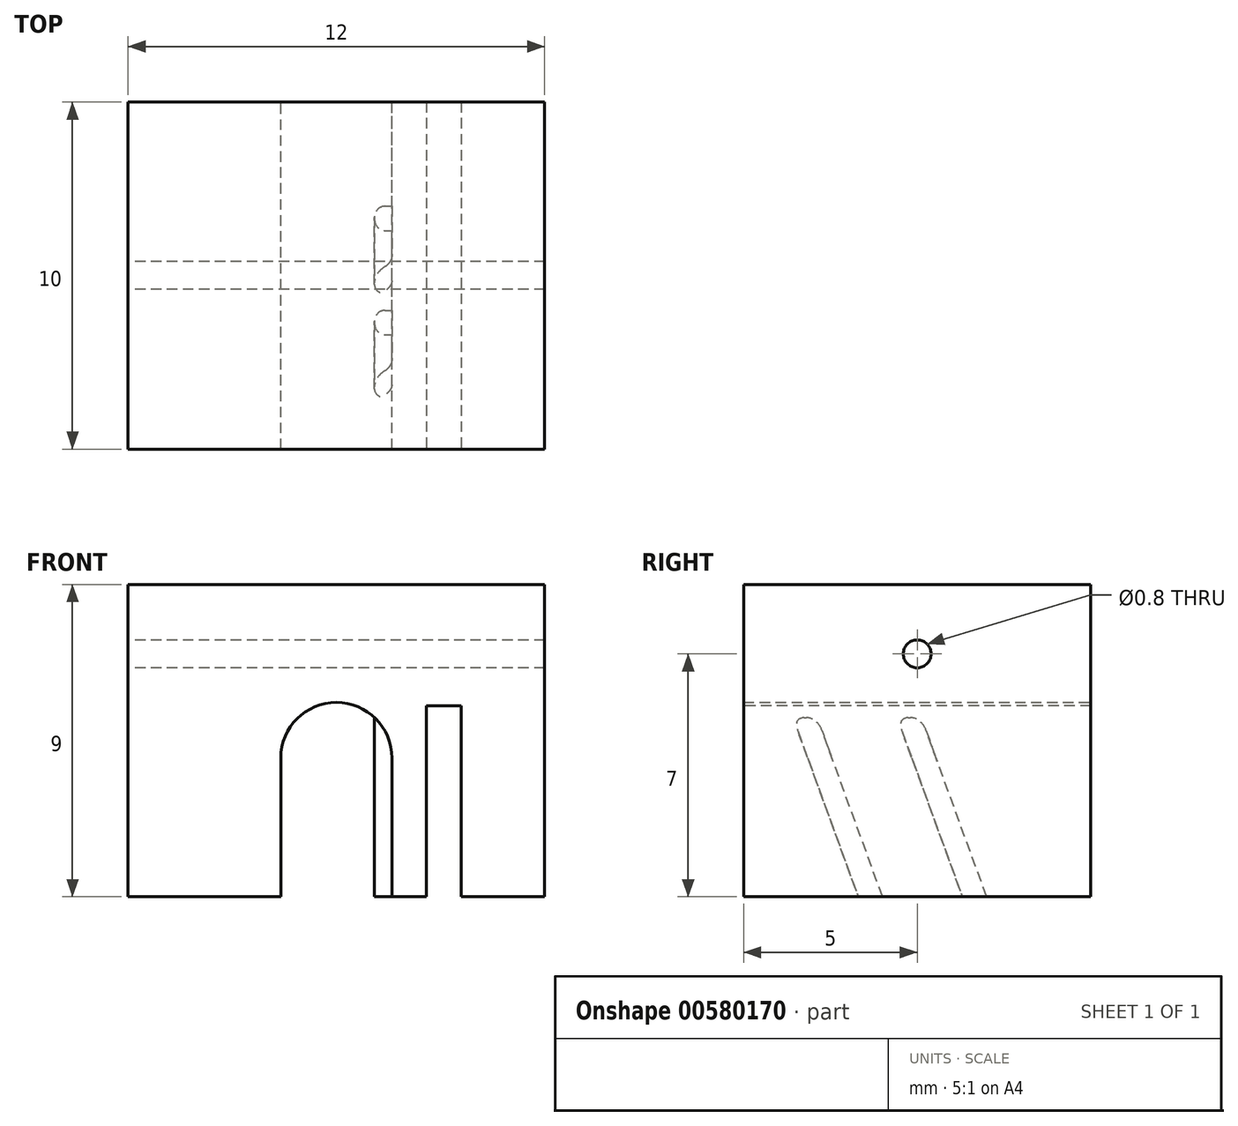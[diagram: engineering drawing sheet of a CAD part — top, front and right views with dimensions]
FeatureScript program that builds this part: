
annotation { "Feature Type Name" : "Feature", "Feature Type Description" : "" }
export const myFeature = defineFeature(function(context is Context, id is Id, definition is map)
    precondition{}
    {
        {
            var Q0;
            Q0=qCreatedBy(makeId("Front.planeOp"),FACE);
            var sketch = newSketch(context, id + "F0", { "sketchPlane" : qUnion([Q0])});
            skLineSegment(sketch, "E0", {"start": v(0, 0) * mm, "end": v(0, 6.31) * mm, "construction": true});
            skLineSegment(sketch, "E1.bottom", {"start": v(-6, 0) * mm, "end": v(-1.6, 0) * mm});
            skLineSegment(sketch, "E1.top", {"start": v(-6, 9) * mm, "end": v(6, 9) * mm});
            skLineSegment(sketch, "E1.left", {"start": v(-6, 0) * mm, "end": v(-6, 9) * mm});
            skLineSegment(sketch, "E1.right", {"start": v(6, 0) * mm, "end": v(6, 9) * mm});
            skArc(sketch, "E2", {"start": v(1.6, 4) * mm, "mid": v(0, 5.6) * mm, "end": v(-1.6, 4) * mm});
            skLineSegment(sketch, "E3", {"start": v(-1.6, 4) * mm, "end": v(-1.6, 0) * mm});
            skLineSegment(sketch, "E4", {"start": v(1.6, 4) * mm, "end": v(1.6, 0) * mm});
            skLineSegment(sketch, "E5.trimOffspring", {"start": v(1.6, 0) * mm, "end": v(6, 0) * mm});
            skSolve(sketch);
        }
        {
            var Q0;
            Q0=makeQuery(id+"F0.imprint","IMPRINT",FACE,{"disambiguationData":[TD([[makeQuery(id+"F0.imprint","IMPRINT",EDGE,{"derivedFrom":sQuery(id+"F0.wireOp",EDGE,"E1.bottom")}),1.0]])]});
            extrude(context, id + "F1", {"entities" : qUnion([Q0]), "depth" : 10 * mm, "offsetDistance" : 25 * mm});
        }
        {
            var Q0;
            Q0=makeQuery(id+"F1.opExtrude","SWEPT_FACE",FACE,{"disambiguationData":[OSD([sQuery(id+"F0.wireOp",EDGE,"E4")])]});
            var sketch = newSketch(context, id + "F2", { "sketchPlane" : qUnion([Q0])});
            skLineSegment(sketch, "E6", {"start": v(3, 0) * mm, "end": v(5.18, 6) * mm});
            skLineSegment(sketch, "E7", {"start": v(5.18, 6) * mm, "end": v(5.88, 6) * mm});
            skLineSegment(sketch, "E8", {"start": v(5.88, 6) * mm, "end": v(3.7, 0) * mm});
            skLineSegment(sketch, "E9", {"start": v(3.7, 0) * mm, "end": v(3, 0) * mm});
            skLineSegment(sketch, "E10.1.0.0", {"start": v(6.7, 0) * mm, "end": v(6, 0) * mm});
            skLineSegment(sketch, "E10.1.0.1", {"start": v(6, 0) * mm, "end": v(8.18, 6) * mm});
            skLineSegment(sketch, "E10.1.0.2", {"start": v(8.18, 6) * mm, "end": v(8.88, 6) * mm});
            skLineSegment(sketch, "E10.1.0.3", {"start": v(8.88, 6) * mm, "end": v(6.7, 0) * mm});
            skLineSegment(sketch, "E10.direction1", {"start": v(3, 0) * mm, "end": v(6, 0) * mm, "construction": true});
            skSolve(sketch);
        }
        {
            var Q0;
            Q0 = qSketchRegion(id + "F2", true);
            extrude(context, id + "F3", {"entities" : qUnion([Q0]), "operationType" : NewBodyOperationType.ADD, "depth" : 0.5 * mm, "offsetDistance" : 25 * mm});
        }
        {
            var Q0;
            Q0=makeQuery(id+"F3.opExtrude","CAP_EDGE",EDGE,{"disambiguationData":[OSD([sQuery(id+"F2.wireOp",EDGE,"E6")])],"isStart":false});
            var Q1;
            Q1=makeQuery(id+"F3.opExtrude","CAP_EDGE",EDGE,{"disambiguationData":[OSD([sQuery(id+"F2.wireOp",EDGE,"E8")])],"isStart":false});
            var Q2;
            Q2=makeQuery(id+"F3.opExtrude","CAP_EDGE",EDGE,{"disambiguationData":[OSD([sQuery(id+"F2.wireOp",EDGE,"E10.1.0.1")])],"isStart":false});
            var Q3;
            Q3=makeQuery(id+"F3.opExtrude","CAP_EDGE",EDGE,{"disambiguationData":[OSD([sQuery(id+"F2.wireOp",EDGE,"E10.1.0.3")])],"isStart":false});
            fillet(context, id + "F4", {"entities" : qUnion([Q0, Q1, Q2, Q3]), "tangentPropagation" : true, "radius" : 0.3 * mm, "defaultsChanged" : false, "vertexSettings" : [], "allowEdgeOverflow" : false});
        }
        {
            var Q0;
            Q0=makeQuery(id+"F3.boolean.opBoolean","MERGE",FACE,{"derivedFrom":[makeQuery(id+"F1.opExtrude","SWEPT_FACE",FACE,{"disambiguationData":[OSD([sQuery(id+"F0.wireOp",EDGE,"E5.trimOffspring")])]}),makeQuery(id+"F3.opExtrude","SWEPT_FACE",FACE,{"disambiguationData":[OSD([sQuery(id+"F2.wireOp",EDGE,"E9")])]}),makeQuery(id+"F3.opExtrude","SWEPT_FACE",FACE,{"disambiguationData":[OSD([sQuery(id+"F2.wireOp",EDGE,"E10.1.0.0")])]})]});
            var sketch = newSketch(context, id + "F5", { "sketchPlane" : qUnion([Q0])});
            skLineSegment(sketch, "E11.bottom", {"start": v(3.6, 0) * mm, "end": v(2.6, 0) * mm});
            skLineSegment(sketch, "E11.top", {"start": v(3.6, 10) * mm, "end": v(2.6, 10) * mm});
            skLineSegment(sketch, "E11.left", {"start": v(3.6, 0) * mm, "end": v(3.6, 10) * mm});
            skLineSegment(sketch, "E11.right", {"start": v(2.6, 0) * mm, "end": v(2.6, 10) * mm});
            skSolve(sketch);
        }
        {
            var Q0;
            Q0=makeQuery(id+"F5.imprint","IMPRINT",FACE,{"disambiguationData":[TD([[makeQuery(id+"F5.imprint","IMPRINT",EDGE,{"derivedFrom":sQuery(id+"F5.wireOp",EDGE,"E11.bottom")}),1.0]])]});
            extrude(context, id + "F6", {"entities" : qUnion([Q0]), "operationType" : NewBodyOperationType.REMOVE, "oppositeDirection" : true, "depth" : 5.5 * mm, "offsetDistance" : 25 * mm});
        }
        {
            var Q0;
            Q0=makeQuery(id+"F1.opExtrude","SWEPT_FACE",FACE,{"disambiguationData":[OSD([sQuery(id+"F0.wireOp",EDGE,"E1.left")])]});
            var sketch = newSketch(context, id + "F7", { "sketchPlane" : qUnion([Q0])});
            skLineSegment(sketch, "E12", {"start": v(5, 9) * mm, "end": v(5, 0) * mm, "construction": true});
            skCircle(sketch, "E13", {"center": v(5, 7) * mm, "radius": 0.4 * mm});
            skSolve(sketch);
        }
        {
            var Q0;
            Q0=makeQuery(id+"F7.imprint","IMPRINT",FACE,{"disambiguationData":[TD([[makeQuery(id+"F7.imprint","IMPRINT",EDGE,{"derivedFrom":sQuery(id+"F7.wireOp",EDGE,"KUtD91Uf-adPl-PtHf-uWDS-y92F0BOasP55.bottom")}),1.0]])]});
            var Q1;
            Q1=makeQuery(id+"F7.imprint","IMPRINT",FACE,{"disambiguationData":[TD([[makeQuery(id+"F7.imprint","IMPRINT",EDGE,{"derivedFrom":sQuery(id+"F7.wireOp",EDGE,"E13")}),1.0]])]});
            extrude(context, id + "F8", {"entities" : qUnion([Q0, Q1]), "operationType" : NewBodyOperationType.REMOVE, "endBound" : BoundingType.THROUGH_ALL, "oppositeDirection" : true, "depth" : 25 * mm, "offsetDistance" : 25 * mm});
        }
    });
